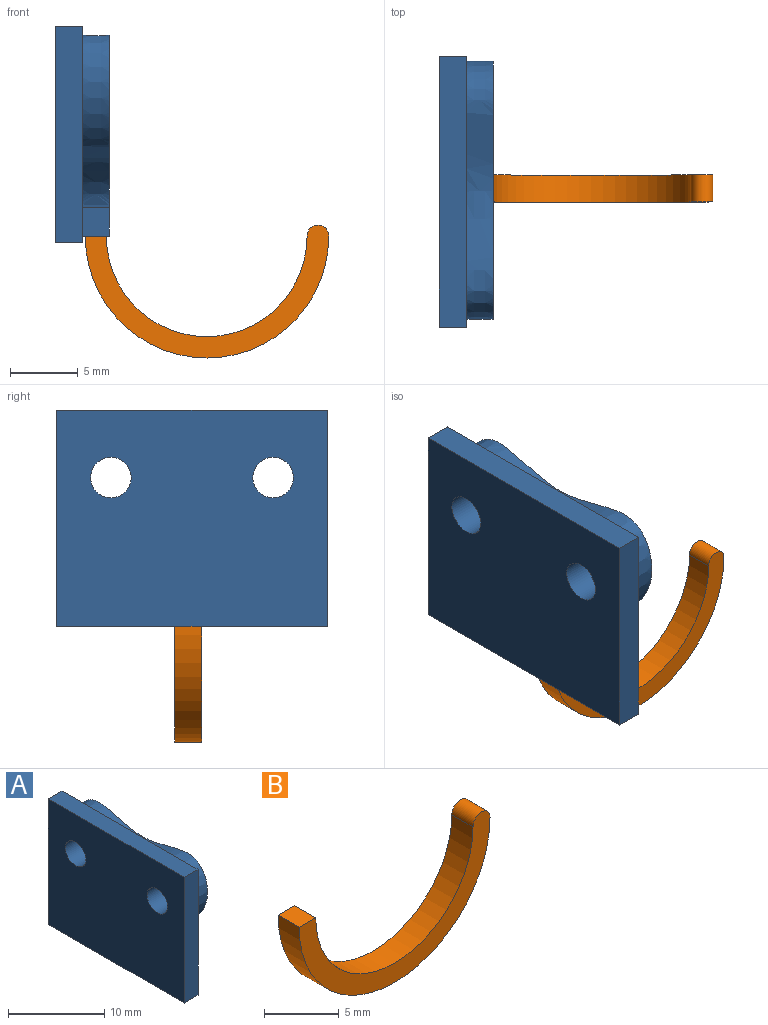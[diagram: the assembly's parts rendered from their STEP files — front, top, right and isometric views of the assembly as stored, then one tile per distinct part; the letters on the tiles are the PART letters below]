
ASSEMBLY  parts=2 mates=1
PART A: 13 faces, bbox 4x20x16 mm
  f0: plane 20x16mm, normal (1,0,0), area 153.8mm2, adj f1,f2,f3,f4,f6,f7,f8,f9
  f1: plane 20x2mm, normal (0,0,-1), area 40mm2, adj f0,f2,f4,f5
  f2: plane 16x2mm, normal (0,1,0), area 32mm2, adj f0,f1,f3,f5
  f3: plane 20x2mm, normal (0,0,1), area 40mm2, adj f0,f2,f4,f5
  f4: plane 16x2mm, normal (0,-1,0), area 32mm2, adj f0,f1,f3,f5
  f5: plane 20x16mm, normal (-1,0,0), area 305.9mm2, adj f1,f2,f3,f4,f11,f12
  f6: plane 2.14x2mm, normal (0,-1,0), area 4.3mm2, adj f0,f7,f9,f10
  f7: plane 2x2mm, normal (0,0,-1), area 4mm2, adj f0,f6,f8,f10
  f8: plane 2.14x2mm, normal (0,1,0), area 4.3mm2, adj f0,f7,f9,f10
  f9: extruded ~19.06x12.68mm, area 100.6mm2, adj f0,f6,f8,f10
  f10: plane 19.5x15.08mm, normal (1,0,0), area 152.1mm2, adj f6,f7,f8,f9,f11,f12
  f11: cylinder r=1.5mm len=4mm, axis (1,0,0), area 37.7mm2, adj f5,f10
  f12: cylinder r=1.5mm len=4mm, axis (1,0,0), area 37.7mm2, adj f5,f10
PART B: 6 faces, bbox 18x2x9.8 mm
  f0: plane 2x1.56mm, normal (0,0,1), area 3.1mm2, adj f1,f3,f4,f5
  f1: cylinder r=9mm len=18mm, axis (0,1,0), area 56.5mm2, adj f0,f2,f4,f5
  f2: cylinder r=0.8mm len=2mm, axis (0,1,0), area 5.1mm2, adj f1,f3,f4,f5
  f3: cylinder r=7.42mm len=14.84mm, axis (0,1,0), area 46.6mm2, adj f0,f2,f4,f5
  f4: plane 18x9.82mm, normal (0,-1,0), area 41.8mm2, adj f0,f1,f2,f3
  f5: plane 18x9.82mm, normal (0,1,0), area 41.8mm2, adj f0,f1,f2,f3
PLACE A t=(-8.28,10.8,-11.61)mm
PLACE B t=(-6.06,2.08,-11.15)mm
MATE fastened A.f7 <-> B.f0  axis (0,0,-1) through (-5.28,1.08,-11.15)mm
